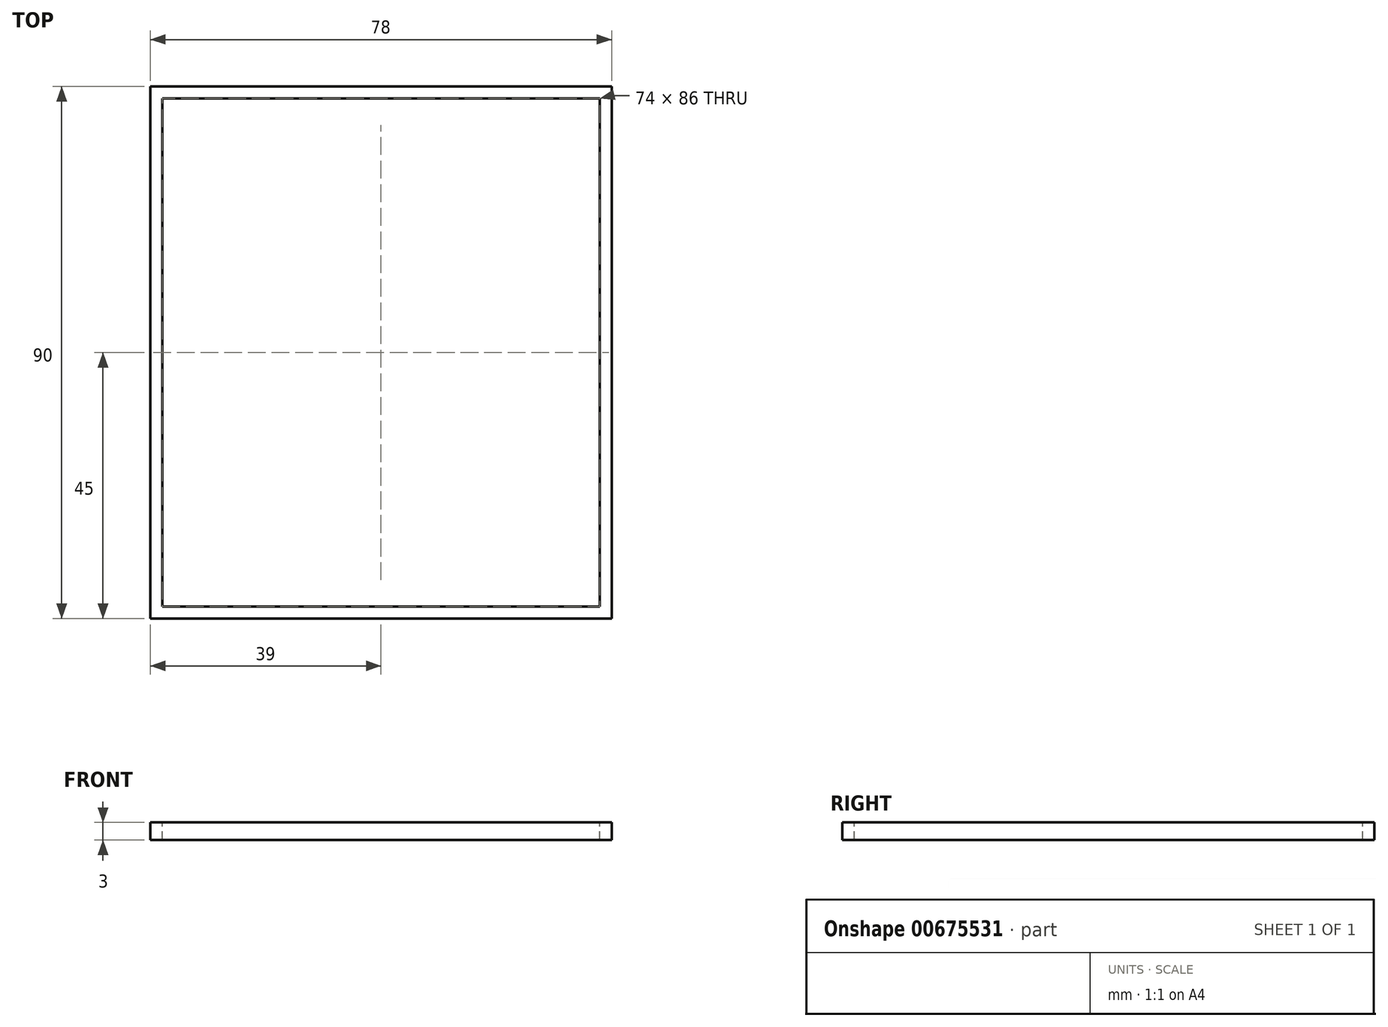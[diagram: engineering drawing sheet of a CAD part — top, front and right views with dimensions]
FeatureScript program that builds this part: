
annotation { "Feature Type Name" : "Feature", "Feature Type Description" : "" }
export const myFeature = defineFeature(function(context is Context, id is Id, definition is map)
    precondition{}
    {
        {
            var Q0;
            Q0=qCreatedBy(makeId("Top.planeOp"),FACE);
            var sketch = newSketch(context, id + "F0", { "sketchPlane" : qUnion([Q0])});
            skLineSegment(sketch, "E0.bottom", {"start": v(-39, 45) * mm, "end": v(39, 45) * mm});
            skLineSegment(sketch, "E0.top", {"start": v(-39, -45) * mm, "end": v(39, -45) * mm});
            skLineSegment(sketch, "E0.left", {"start": v(-39, 45) * mm, "end": v(-39, -45) * mm});
            skLineSegment(sketch, "E0.right", {"start": v(39, 45) * mm, "end": v(39, -45) * mm});
            skSolve(sketch);
        }
        {
            var Q0;
            Q0=qSketchRegion(id+"F0",true);
            extrude(context, id + "F1", {"entities" : qUnion([Q0]), "depth" : 3 * mm, "offsetDistance" : 25 * mm});
        }
        {
            var Q0;
            Q0=makeQuery(id+"F1.opExtrude","CAP_FACE",FACE,{"disambiguationData":[OSD([sQuery(id+"F0.wireOp",EDGE,"E0.bottom"),sQuery(id+"F0.wireOp",EDGE,"E0.top"),sQuery(id+"F0.wireOp",EDGE,"E0.left"),sQuery(id+"F0.wireOp",EDGE,"E0.right")])],"isStart":false});
            var sketch = newSketch(context, id + "F2", { "sketchPlane" : qUnion([Q0])});
            skLineSegment(sketch, "E1.0", {"start": v(-37, 43) * mm, "end": v(-37, -43) * mm});
            skLineSegment(sketch, "E1.1", {"start": v(37, 43) * mm, "end": v(-37, 43) * mm});
            skLineSegment(sketch, "E1.2", {"start": v(37, -43) * mm, "end": v(37, 43) * mm});
            skLineSegment(sketch, "E1.3", {"start": v(-37, -43) * mm, "end": v(37, -43) * mm});
            skSolve(sketch);
        }
        {
            var Q0;
            Q0=qSketchRegion(id+"F2",true);
            extrude(context, id + "F3", {"entities" : qUnion([Q0]), "operationType" : NewBodyOperationType.REMOVE, "endBound" : BoundingType.THROUGH_ALL, "oppositeDirection" : true, "depth" : 25 * mm, "offsetDistance" : 25 * mm});
        }
    });
